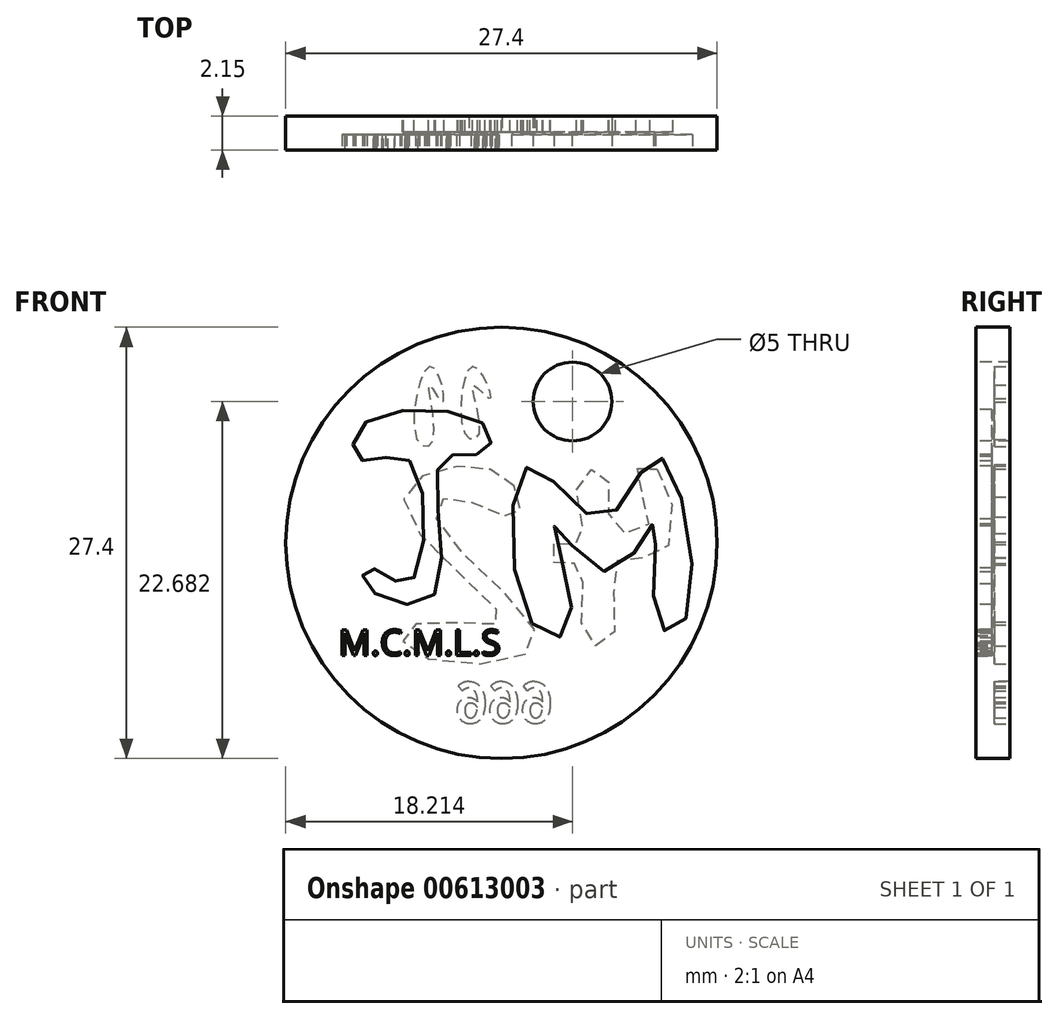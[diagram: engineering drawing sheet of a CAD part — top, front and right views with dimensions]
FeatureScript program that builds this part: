
annotation { "Feature Type Name" : "Feature", "Feature Type Description" : "" }
export const myFeature = defineFeature(function(context is Context, id is Id, definition is map)
    precondition{}
    {
        {
            var Q0;
            Q0=qCreatedBy(makeId("Front.planeOp"),FACE);
            var sketch = newSketch(context, id + "F0", { "sketchPlane" : qUnion([Q0])});
            skCircle(sketch, "E0", {"center": v(0, 0) * mm, "radius": 13.7 * mm});
            skSolve(sketch);
        }
        {
            var Q0;
            Q0=makeQuery(id+"F0.imprint","IMPRINT",FACE,{"disambiguationData":[TD([[makeQuery(id+"F0.imprint","IMPRINT",EDGE,{"derivedFrom":sQuery(id+"F0.wireOp",EDGE,"E0")}),1.0]])]});
            extrude(context, id + "F1", {"entities" : qUnion([Q0]), "depth" : 2.15 * mm, "offsetDistance" : 25 * mm});
        }
        {
            var Q0;
            Q0=makeQuery(id+"F1.opExtrude","CAP_FACE",FACE,{"disambiguationData":[OSD([sQuery(id+"F0.wireOp",EDGE,"E0")])],"isStart":false});
            var sketch = newSketch(context, id + "F2", { "sketchPlane" : qUnion([Q0])});
            skCircle(sketch, "E1", {"center": v(4.51, 8.98) * mm, "radius": 2.5 * mm});
            skSolve(sketch);
        }
        {
            var Q0;
            Q0=makeQuery(id+"F2.imprint","IMPRINT",FACE,{"disambiguationData":[TD([[makeQuery(id+"F2.imprint","IMPRINT",EDGE,{"derivedFrom":sQuery(id+"F2.wireOp",EDGE,"E1")}),1.0]])]});
            extrude(context, id + "F3", {"entities" : qUnion([Q0]), "operationType" : NewBodyOperationType.REMOVE, "endBound" : BoundingType.UP_TO_NEXT, "oppositeDirection" : true, "depth" : 25 * mm, "offsetDistance" : 25 * mm});
        }
        {
            var Q0;
            Q0=makeQuery(id+"F1.opExtrude","CAP_FACE",FACE,{"disambiguationData":[OSD([sQuery(id+"F0.wireOp",EDGE,"E0")])],"isStart":false});
            var sketch = newSketch(context, id + "F4", { "sketchPlane" : qUnion([Q0])});
            skFitSpline(sketch, "E2", {"points": [v(-5.84, 5.25) * mm, v(-5.84, -2.51) * mm, v(-8.28, -1.6) * mm, v(-8.73, -2.51) * mm, v(-4.4, -3.43) * mm, v(-3.86, 5.18) * mm, v(-1.2, 5.7) * mm, v(-1.04, 7.46) * mm, v(-8.89, 7.46) * mm, v(-8.89, 5.25) * mm, v(-5.84, 5.25) * mm]});
            skSolve(sketch);
        }
        {
            var Q0;
            Q0=makeQuery(id+"F4.imprint","IMPRINT",FACE,{"disambiguationData":[TD([[makeQuery(id+"F4.imprint","IMPRINT",EDGE,{"derivedFrom":sQuery(id+"F4.wireOp",EDGE,"E2")}),1.0]])]});
            extrude(context, id + "F5", {"entities" : qUnion([Q0]), "operationType" : NewBodyOperationType.REMOVE, "oppositeDirection" : true, "depth" : 1 * mm, "offsetDistance" : 25 * mm});
        }
        {
            var Q0;
            Q0=makeQuery(id+"F1.opExtrude","CAP_FACE",FACE,{"disambiguationData":[OSD([sQuery(id+"F0.wireOp",EDGE,"E0")])],"isStart":false});
            var sketch = newSketch(context, id + "F6", { "sketchPlane" : qUnion([Q0])});
            skFitSpline(sketch, "E3", {"points": [v(1.93, -5.1) * mm, v(1.77, 4.87) * mm, v(6.42, 1.52) * mm, v(9.92, 5.48) * mm, v(11.75, -4.72) * mm, v(10, -5.18) * mm, v(9.7, 1.22) * mm, v(6.87, -1.83) * mm, v(3.37, 1.06) * mm, v(4.36, -5.26) * mm, v(1.93, -5.1) * mm]});
            skSolve(sketch);
        }
        {
            var Q0;
            Q0=makeQuery(id+"F6.imprint","IMPRINT",FACE,{"disambiguationData":[TD([[makeQuery(id+"F6.imprint","IMPRINT",EDGE,{"derivedFrom":sQuery(id+"F6.wireOp",EDGE,"E3")}),-1.0]])]});
            extrude(context, id + "F7", {"entities" : qUnion([Q0]), "operationType" : NewBodyOperationType.REMOVE, "oppositeDirection" : true, "depth" : 1 * mm, "offsetDistance" : 25 * mm});
        }
        {
            var Q0;
            Q0=makeQuery(id+"F1.opExtrude","CAP_FACE",FACE,{"disambiguationData":[OSD([sQuery(id+"F0.wireOp",EDGE,"E0")])],"isStart":false});
            var sketch = newSketch(context, id + "F8", { "sketchPlane" : qUnion([Q0])});
            skText(sketch, "E4", { "text": "M.C.M.L.S", "fontName": "OpenSans-Regular.ttf"});
            const initialGuessF8  = {"E4": [-0.01034, -0.00713, 1, 0, 0.00162]};
            skSetInitialGuess(sketch, initialGuessF8);
            skSolve(sketch);
        }
        {
            var Q0;
            Q0 = qSketchRegion(id + "F8", true);
            extrude(context, id + "F9", {"entities" : qUnion([Q0]), "operationType" : NewBodyOperationType.REMOVE, "oppositeDirection" : true, "depth" : 1 * mm, "offsetDistance" : 25 * mm});
        }
        {
            var Q0;
            Q0=makeQuery(id+"F1.opExtrude","CAP_FACE",FACE,{"disambiguationData":[OSD([sQuery(id+"F0.wireOp",EDGE,"E0")])],"isStart":true});
            var sketch = newSketch(context, id + "F10", { "sketchPlane" : qUnion([Q0])});
            skFitSpline(sketch, "E5", {"points": [v(-9.9, 4.7) * mm, v(-10.27, -0.63) * mm, v(-7.3, -1.17) * mm, v(-7.04, -6.01) * mm, v(-5.32, -6.07) * mm, v(-5, -1.44) * mm, v(-3.43, -1.33) * mm, v(-3.38, 0) * mm, v(-5.1, 0) * mm, v(-4.89, 4.06) * mm, v(-6.6, 4.38) * mm, v(-7.1, 0.99) * mm, v(-9.36, 1.2) * mm, v(-8.55, 4.54) * mm, v(-9.9, 4.7) * mm]});
            skFitSpline(sketch, "E6", {"points": [v(-0.8, 3.62) * mm, v(3.24, 4.8) * mm, v(6.15, 2.17) * mm, v(0, -4.94) * mm, v(5.61, -5.2) * mm, v(5.77, -6.87) * mm, v(-2.2, -6.39) * mm, v(4, 1.26) * mm, v(3.24, 2.92) * mm, v(-0.9, 1.69) * mm, v(-0.8, 3.62) * mm]});
            skFitSpline(sketch, "E7", {"points": [v(0.93, 10.14) * mm, v(1.95, 11.16) * mm, v(2.27, 6.85) * mm, v(1.41, 6.9) * mm, v(1.79, 10.03) * mm, v(0.77, 9.17) * mm, v(0.93, 10.14) * mm]});
            skFitSpline(sketch, "E8", {"points": [v(3.78, 10.03) * mm, v(4.64, 11.16) * mm, v(5.34, 6.53) * mm, v(4.37, 6.42) * mm, v(4.59, 10.03) * mm, v(3.78, 8.95) * mm, v(3.78, 10.03) * mm]});
            skText(sketch, "E9", { "text": "666", "fontName": "NotoSansCJKjp-Bold.otf"});
            const initialGuessF10  = {"E9": [-0.00327, -0.01145, 1, 0, 0.00253]};
            skSetInitialGuess(sketch, initialGuessF10);
            skSolve(sketch);
        }
        {
            var Q0;
            Q0 = qSketchRegion(id + "F10", true);
            extrude(context, id + "F11", {"entities" : qUnion([Q0]), "operationType" : NewBodyOperationType.REMOVE, "oppositeDirection" : true, "depth" : 1 * mm, "offsetDistance" : 25 * mm});
        }
    });
